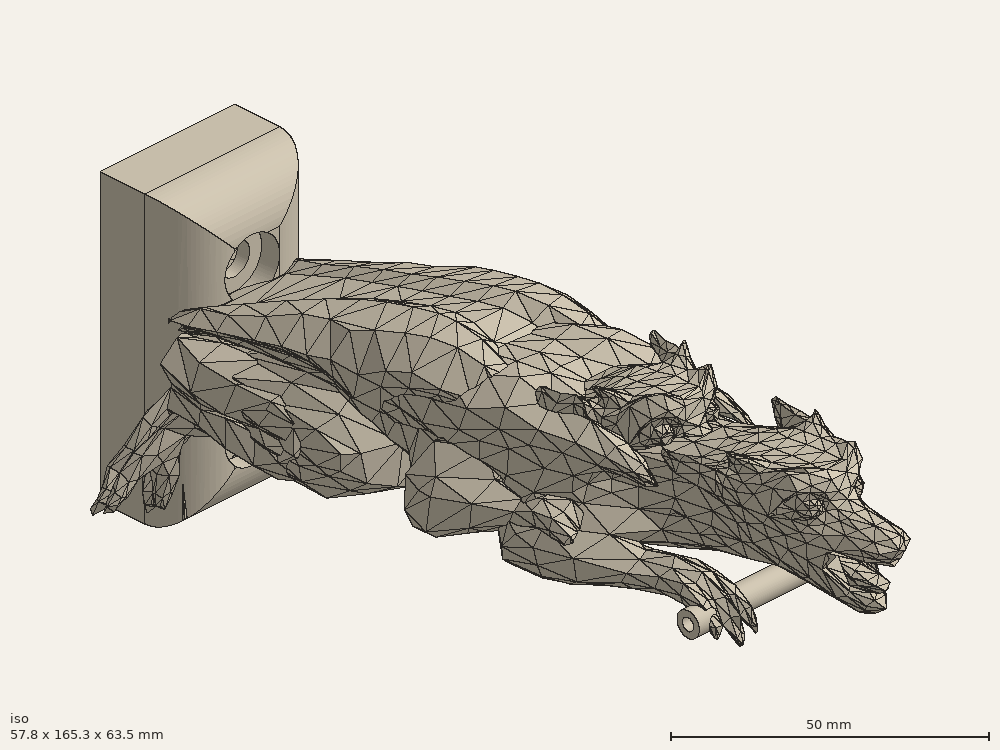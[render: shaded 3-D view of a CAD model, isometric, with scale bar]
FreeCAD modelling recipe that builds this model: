
FCSTD DOCUMENT  (FreeCAD 1.0R1.0rc2)
Label: RemeshLampHolder
License: All rights reserved
LicenseURL: http://en.wikipedia.org/wiki/All_rights_reserved
objects: Part::Cylinder×5, Part::MultiFuse×4, Part::Feature×3, Mesh::Feature×2, Part::FeaturePython×2, Part::Cut×2, Part::Box×1, Part::Fillet×1
note: 18 computed .brp shape members not serialized (recipe doc carries the construction recipe); baked Part::Feature solids carry a one-line shape summary decoded from their .brp

FEATURE [Mesh::Feature] gargoyle_1
  Placement = pos=(0,0,28) rot=(1,0,0;-0.279253rad)
FEATURE [Part::Cylinder] Cylinder013
  Angle = 360
  AttacherType = Attacher::AttachEngine3D
  FirstAngle = 0
  Height = 10
  Placement = pos=(0,-10,0) rot=(1,0,0;1.5708rad)
  Radius = 6
  SecondAngle = 0
FEATURE [Part::Cylinder] Cylinder014
  Angle = 360
  AttacherType = Attacher::AttachEngine3D
  FirstAngle = 0
  Height = 30
  Placement = pos=(0,10,0) rot=(1,0,0;1.5708rad)
  Radius = 3.3
  SecondAngle = 0
FEATURE [Part::Cylinder] Cylinder015
  Angle = 360
  AttacherType = Attacher::AttachEngine3D
  FirstAngle = 0
  Height = 10
  Placement = pos=(0,-10,0) rot=(1,0,0;1.5708rad)
  Radius = 6
  SecondAngle = 0
FEATURE [Part::Cylinder] Cylinder016
  Angle = 360
  AttacherType = Attacher::AttachEngine3D
  FirstAngle = 0
  Height = 30
  Placement = pos=(0,10,0) rot=(1,0,0;1.5708rad)
  Radius = 3.3
  SecondAngle = 0
FEATURE [Part::MultiFuse] Fusion006
  Placement = pos=(15,30,15) rot=(0,0,1;0rad)
  Shapes = -> [Cylinder014,Cylinder013]
FEATURE [Part::MultiFuse] Fusion007
  Placement = pos=(15,30,45) rot=(0,0,1;0rad)
  Shapes = -> [Cylinder016,Cylinder015]
FEATURE [Part::MultiFuse] Fusion
  Placement = pos=(14,99,0) rot=(0,0,1;0rad)
  Shapes = -> [Fusion007,Fusion006]
FEATURE [Part::Box] Box  label="Cube"
  AttacherType = Attacher::AttachEngine3D
  Height = 60
  Length = 30
  Placement = pos=(15,115,0) rot=(0,0,1;0rad)
  Width = 20
FEATURE [Part::FeaturePython] Tube  # WARN: FeaturePython — macro-defined, semantics opaque (R4)
  AttacherType = Attacher::AttachEngine3D
  Height = 40
  InnerRadius = 1.25
  OuterRadius = 2.5
  Placement = pos=(9,-2,36) rot=(0,1,0;1.5708rad)
FEATURE [Part::Cylinder] Cylinder
  Angle = 360
  AttacherType = Attacher::AttachEngine3D
  FirstAngle = 0
  Height = 50
  Placement = pos=(9,-2,36) rot=(0,1,0;1.5708rad)
  Radius = 1.25
  SecondAngle = 0
FEATURE [Part::Feature] gargoyle_002_solid  label="gargoyle_002 (Solid)"
  shape: bbox 57.79 x 129.5 x 61.96 mm, 2729 faces (baked)
FEATURE [Mesh::Feature] Mesh  label="gargoyle_002 (Solid) (Meshed)"
FEATURE [Part::Feature] Mesh001
  shape: bbox 56.51 x 126.2 x 55.4 mm, 2657 faces, 0 solids (baked)
FEATURE [Part::Feature] Mesh001_solid  label="Mesh001 (Solid)"
  shape: bbox 56.51 x 126.2 x 55.4 mm, 2653 faces (baked)
FEATURE [Part::Fillet] Fillet
  Base = -> Box
  EdgeLinks = -> Box [Edge1,Edge5,Edge9,Edge10]
  Edges = 4 edges r=10: [Edge1,Edge5,Edge9,Edge10]
FEATURE [Part::FeaturePython] Clone  label="Mesh001 (Solid)001"  # Draft clone (typed FeaturePython)
  AttacherType = Attacher::AttachEngine3D
  Fuse = false
  Objects = -> [Mesh001_solid]
  Placement = pos=(0,-38,0) rot=(0,0,1;0rad)
  Scale = (1,1.3,1)
FEATURE [Part::MultiFuse] Fusion008
  Shapes = -> [Fillet,Clone,Tube]
FEATURE [Part::Cut] Cut
  Base = -> Fusion008
  Tool = -> Cylinder
FEATURE [Part::Cut] Cut001
  Base = -> Cut
  Tool = -> Fusion
